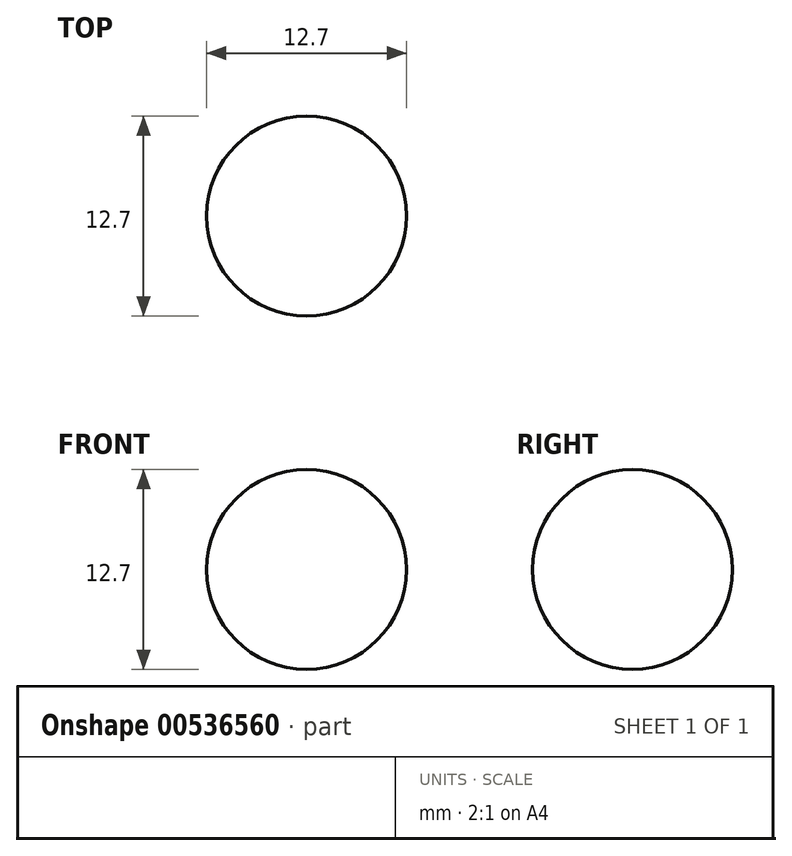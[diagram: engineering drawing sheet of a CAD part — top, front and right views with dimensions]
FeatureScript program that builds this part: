
annotation { "Feature Type Name" : "Feature", "Feature Type Description" : "" }
export const myFeature = defineFeature(function(context is Context, id is Id, definition is map)
    precondition{}
    {
        {
            var Q0;
            Q0=qCreatedBy(makeId("Top.planeOp"),FACE);
            var sketch = newSketch(context, id + "F0", { "sketchPlane" : qUnion([Q0])});
            skCircle(sketch, "E0", {"center": v(0, 0) * mm, "radius": 6.35 * mm, "construction": true});
            skLineSegment(sketch, "E1", {"start": v(-6.35, 0) * mm, "end": v(6.35, 0) * mm});
            skArc(sketch, "E2", {"start": v(6.35, 0) * mm, "mid": v(0, 6.35) * mm, "end": v(-6.35, 0) * mm});
            skSolve(sketch);
        }
        {
            var Q0;
            Q0=makeQuery(id+"F0.imprint","IMPRINT",FACE,{"disambiguationData":[TD([[makeQuery(id+"F0.imprint","IMPRINT",EDGE,{"derivedFrom":sQuery(id+"F0.wireOp",EDGE,"E1")}),1.0]])]});
            var Q1;
            Q1=sQuery(id+"F0.wireOp",EDGE,"E0");
            var Q2;
            Q2=sQuery(id+"F0.wireOp",EDGE,"E1");
            revolve(context, id + "F1", {"entities" : qUnion([Q0]), "surfaceEntities" : qUnion([Q1]), "axis" : qUnion([Q2]), "revolveType" : RevolveType.FULL});
        }
    });
